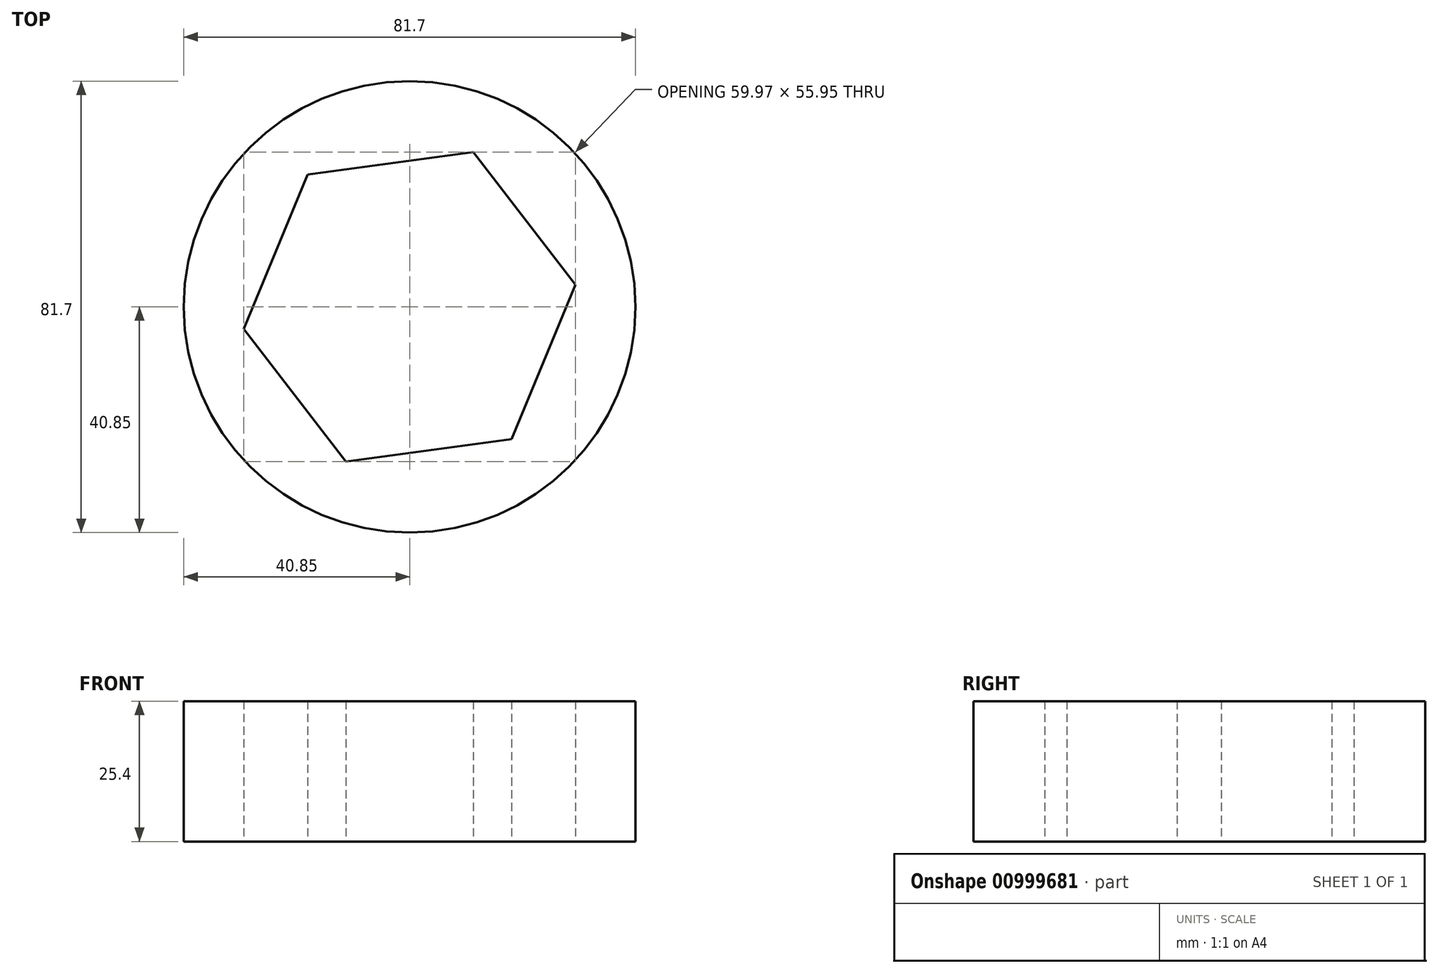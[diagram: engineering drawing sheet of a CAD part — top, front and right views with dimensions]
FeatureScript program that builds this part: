
annotation { "Feature Type Name" : "Feature", "Feature Type Description" : "" }
export const myFeature = defineFeature(function(context is Context, id is Id, definition is map)
    precondition{}
    {
        {
            var Q0;
            Q0=qCreatedBy(makeId("Top.planeOp"),FACE);
            var sketch = newSketch(context, id + "F0", { "sketchPlane" : qUnion([Q0])});
            skCircle(sketch, "E0", {"center": v(0, 0) * mm, "radius": 40.85 * mm});
            skCircle(sketch, "E1.cCircle", {"center": v(0, 0) * mm, "radius": 30.25 * mm, "construction": true});
            skLineSegment(sketch, "E1.0", {"start": v(18.47, -23.96) * mm, "end": v(-11.52, -27.98) * mm});
            skLineSegment(sketch, "E1.1", {"start": v(-11.52, -27.98) * mm, "end": v(-29.99, -4.01) * mm});
            skLineSegment(sketch, "E1.2", {"start": v(-29.99, -4.01) * mm, "end": v(-18.47, 23.96) * mm});
            skLineSegment(sketch, "E1.3", {"start": v(-18.47, 23.96) * mm, "end": v(11.52, 27.98) * mm});
            skLineSegment(sketch, "E1.4", {"start": v(11.52, 27.98) * mm, "end": v(29.99, 4.01) * mm});
            skLineSegment(sketch, "E1.5", {"start": v(29.99, 4.01) * mm, "end": v(18.47, -23.96) * mm});
            skSolve(sketch);
        }
        {
            var Q0;
            Q0 = qSketchRegion(id + "F0", true);
            extrude(context, id + "F1", {"entities" : qUnion([Q0]), "depth" : 25.4 * mm, "offsetDistance" : 25.4 * mm});
        }
    });
